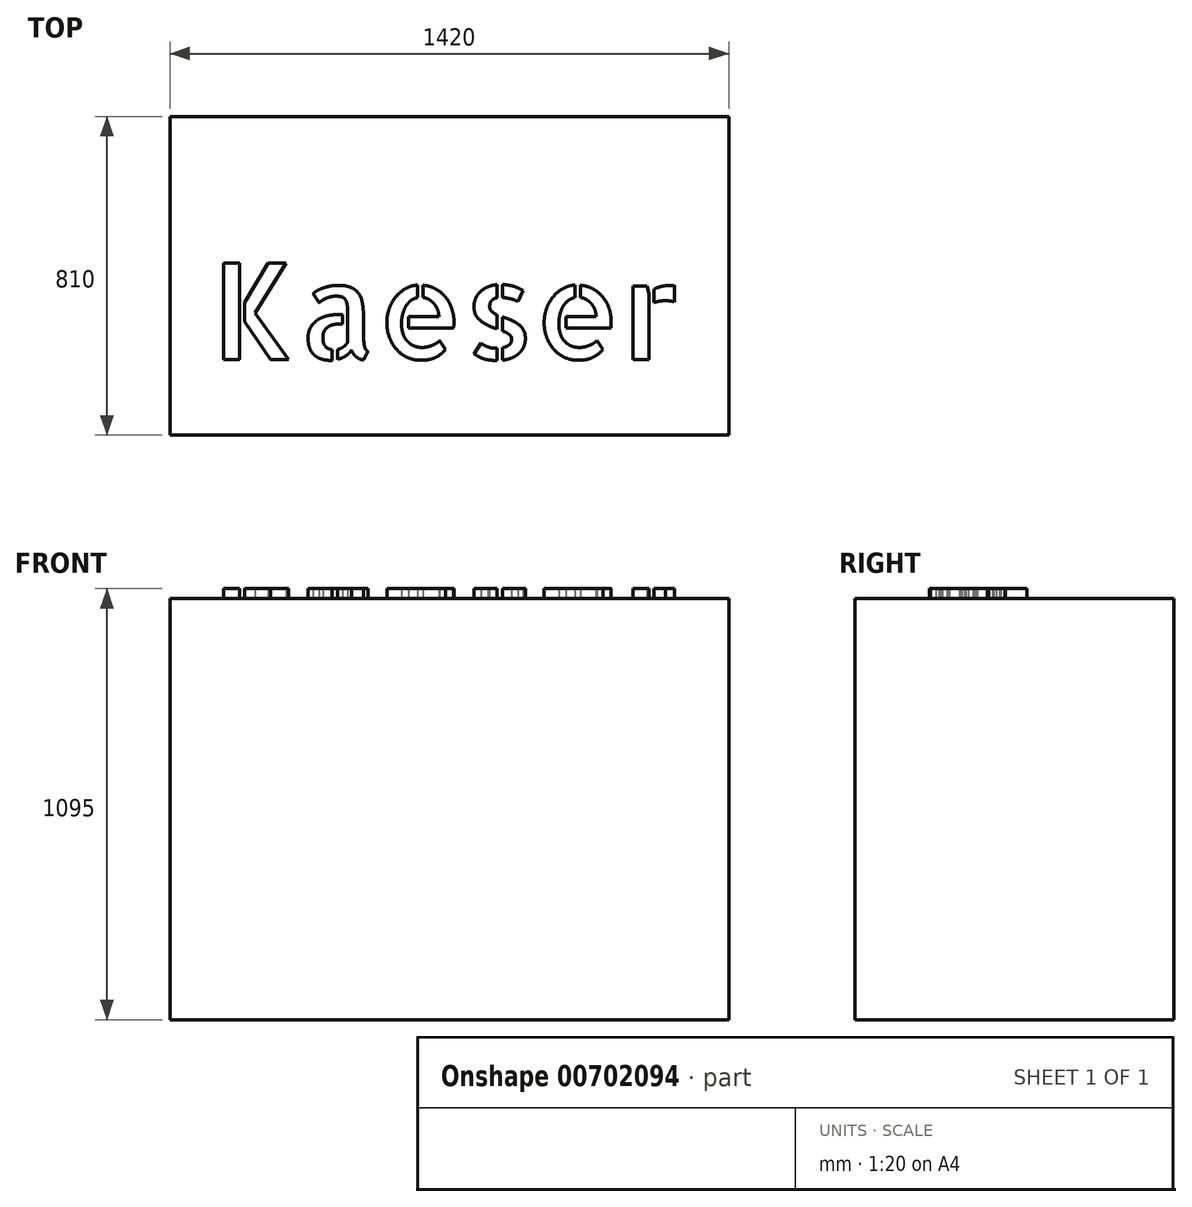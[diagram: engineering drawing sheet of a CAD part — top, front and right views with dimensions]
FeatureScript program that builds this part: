
annotation { "Feature Type Name" : "Feature", "Feature Type Description" : "" }
export const myFeature = defineFeature(function(context is Context, id is Id, definition is map)
    precondition{}
    {
        {
            var Q0;
            Q0=qCreatedBy(makeId("Top.planeOp"),FACE);
            var sketch = newSketch(context, id + "F0", { "sketchPlane" : qUnion([Q0])});
            skLineSegment(sketch, "E0.bottom", {"start": v(0, 0) * mm, "end": v(1420, 0) * mm});
            skLineSegment(sketch, "E0.top", {"start": v(0, 810) * mm, "end": v(1420, 810) * mm});
            skLineSegment(sketch, "E0.left", {"start": v(0, 0) * mm, "end": v(0, 810) * mm});
            skLineSegment(sketch, "E0.right", {"start": v(1420, 0) * mm, "end": v(1420, 810) * mm});
            skSolve(sketch);
        }
        {
            var Q0;
            Q0=makeQuery(id+"F0.imprint","IMPRINT",FACE,{"disambiguationData":[TD([[makeQuery(id+"F0.imprint","IMPRINT",EDGE,{"derivedFrom":sQuery(id+"F0.wireOp",EDGE,"E0.bottom")}),1.0]])]});
            extrude(context, id + "F1", {"entities" : qUnion([Q0]), "depth" : 1070 * mm, "offsetDistance" : 25 * mm});
        }
        {
            var Q0;
            Q0=makeQuery(id+"F1.opExtrude","CAP_FACE",FACE,{"disambiguationData":[OSD([sQuery(id+"F0.wireOp",EDGE,"E0.bottom"),sQuery(id+"F0.wireOp",EDGE,"E0.top"),sQuery(id+"F0.wireOp",EDGE,"E0.left"),sQuery(id+"F0.wireOp",EDGE,"E0.right")])],"isStart":false});
            var sketch = newSketch(context, id + "F2", { "sketchPlane" : qUnion([Q0])});
            skText(sketch, "E1", { "text": "Kaeser", "fontName": "AllertaStencil-Regular.ttf"});
            const initialGuessF2  = {"E1": [0.10476, 0.19163, 1, 0, 0.24552]};
            skSetInitialGuess(sketch, initialGuessF2);
            skSolve(sketch);
        }
        {
            var Q0;
            Q0 = qSketchRegion(id + "F2", true);
            extrude(context, id + "F3", {"entities" : qUnion([Q0]), "operationType" : NewBodyOperationType.ADD, "depth" : 25 * mm, "offsetDistance" : 25 * mm});
        }
    });
